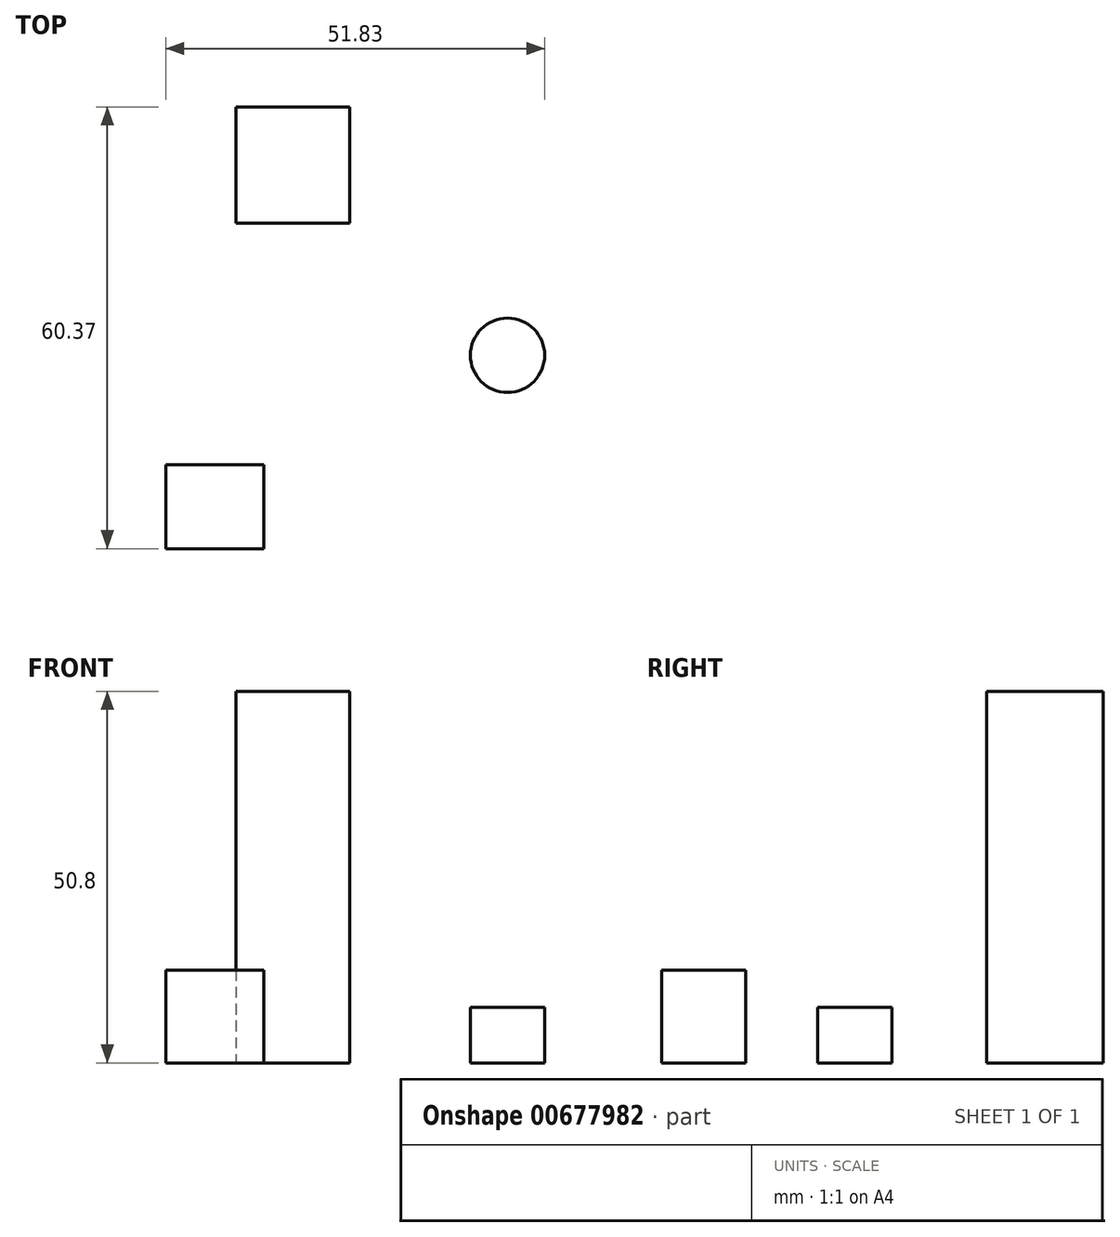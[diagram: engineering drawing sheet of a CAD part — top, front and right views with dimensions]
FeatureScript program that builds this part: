
annotation { "Feature Type Name" : "Feature", "Feature Type Description" : "" }
export const myFeature = defineFeature(function(context is Context, id is Id, definition is map)
    precondition{}
    {
        {
            var Q0;
            Q0=qCreatedBy(makeId("Top.planeOp"),FACE);
            var sketch = newSketch(context, id + "F0", { "sketchPlane" : qUnion([Q0])});
            skLineSegment(sketch, "E0.bottom", {"start": v(-7.8, 12.9) * mm, "end": v(7.8, 12.9) * mm});
            skLineSegment(sketch, "E0.top", {"start": v(-7.8, -3.02) * mm, "end": v(7.8, -3.02) * mm});
            skLineSegment(sketch, "E0.left", {"start": v(-7.8, 12.9) * mm, "end": v(-7.8, -3.02) * mm});
            skLineSegment(sketch, "E0.right", {"start": v(7.8, 12.9) * mm, "end": v(7.8, -3.02) * mm});
            skPoint(sketch, "E0.middle", {"position": v(0, 4.94) * mm});
            skSolve(sketch);
        }
        {
            var Q0;
            Q0=makeQuery(id+"F0.imprint","IMPRINT",FACE,{"disambiguationData":[TD([[makeQuery(id+"F0.imprint","IMPRINT",EDGE,{"derivedFrom":sQuery(id+"F0.wireOp",EDGE,"E0.bottom")}),-1.0]])]});
            extrude(context, id + "F1", {"entities" : qUnion([Q0]), "depth" : 25.4 * mm, "offsetDistance" : 25.4 * mm});
        }
        {
            var Q0;
            Q0=makeQuery(id+"F1.opExtrude","CAP_FACE",FACE,{"disambiguationData":[OSD([sQuery(id+"F0.wireOp",EDGE,"E0.bottom"),sQuery(id+"F0.wireOp",EDGE,"E0.top"),sQuery(id+"F0.wireOp",EDGE,"E0.left"),sQuery(id+"F0.wireOp",EDGE,"E0.right")])],"isStart":false});
            extrude(context, id + "F2", {"entities" : qUnion([Q0]), "operationType" : NewBodyOperationType.ADD, "depth" : 25.4 * mm, "offsetDistance" : 25.4 * mm});
        }
        {
            var Q0;
            Q0=qCreatedBy(makeId("Top.planeOp"),FACE);
            var sketch = newSketch(context, id + "F3", { "sketchPlane" : qUnion([Q0])});
            skLineSegment(sketch, "E1.bottom", {"start": v(-17.37, -47.47) * mm, "end": v(-3.96, -47.47) * mm});
            skLineSegment(sketch, "E1.top", {"start": v(-17.37, -35.98) * mm, "end": v(-3.96, -35.98) * mm});
            skLineSegment(sketch, "E1.left", {"start": v(-17.37, -47.47) * mm, "end": v(-17.37, -35.98) * mm});
            skLineSegment(sketch, "E1.right", {"start": v(-3.96, -47.47) * mm, "end": v(-3.96, -35.98) * mm});
            skSolve(sketch);
        }
        {
            var Q0;
            Q0=makeQuery(id+"F3.imprint","IMPRINT",FACE,{"disambiguationData":[TD([[makeQuery(id+"F3.imprint","IMPRINT",EDGE,{"derivedFrom":sQuery(id+"F3.wireOp",EDGE,"E1.bottom")}),1.0]])]});
            extrude(context, id + "F4", {"entities" : qUnion([Q0]), "depth" : 12.7 * mm, "offsetDistance" : 25.4 * mm});
        }
        {
            var Q0;
            Q0=qCreatedBy(makeId("Top.planeOp"),FACE);
            var sketch = newSketch(context, id + "F5", { "sketchPlane" : qUnion([Q0])});
            skCircle(sketch, "E2", {"center": v(29.38, -21.04) * mm, "radius": 5.08 * mm});
            skSolve(sketch);
        }
        {
            var Q0;
            Q0=makeQuery(id+"F5.imprint","IMPRINT",FACE,{"disambiguationData":[TD([[makeQuery(id+"F5.imprint","IMPRINT",EDGE,{"derivedFrom":sQuery(id+"F5.wireOp",EDGE,"E2")}),1.0]])]});
            extrude(context, id + "F6", {"entities" : qUnion([Q0]), "depth" : 7.62 * mm, "offsetDistance" : 25.4 * mm});
        }
    });
